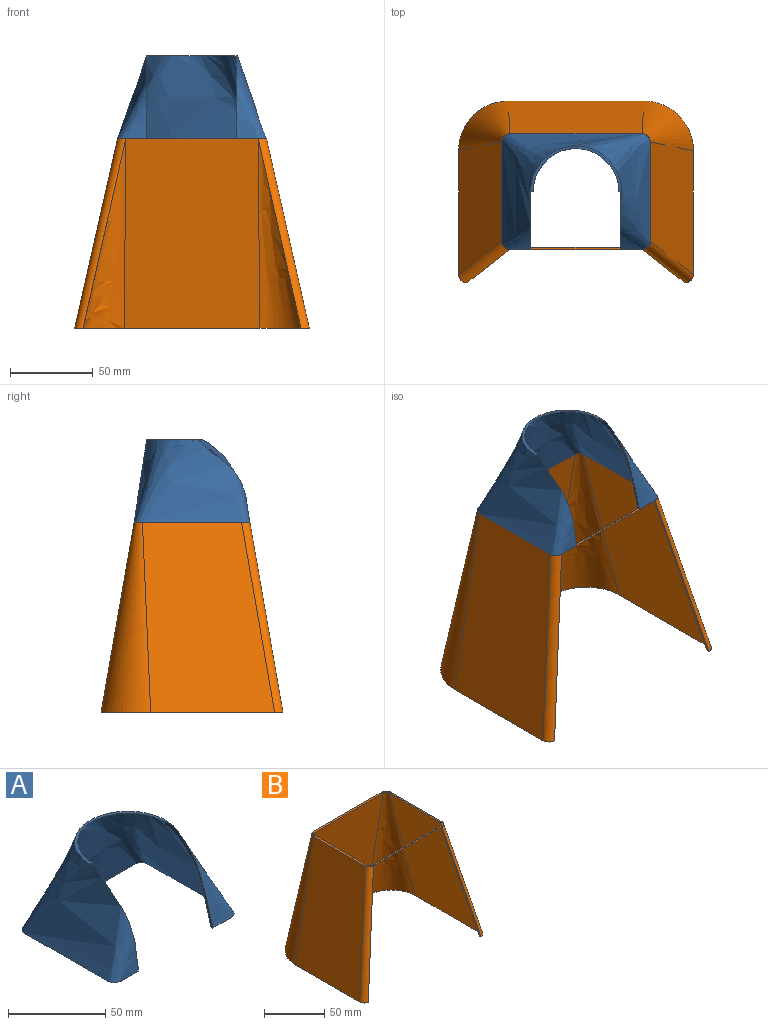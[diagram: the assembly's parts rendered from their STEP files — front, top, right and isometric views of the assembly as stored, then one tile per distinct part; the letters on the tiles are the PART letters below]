
ASSEMBLY  parts=2 mates=1
PART A: 8 faces, bbox 3360.5x2510.9x2276.9 mm
  f0: offset ~1137.38x287.71mm, area 68863mm2, adj f1,f2,f4,f5,f6,f7
  f1: plane 2316.14x2296.14mm, normal (0,0,1), area 367.9mm2, adj f0,f3,f5,f7
  f2: plane 66.45x45.38mm, normal (0,0,-1), area 137.2mm2, adj f0,f3,f4,f5,f6,f7
  f3: bspline ~90x70mm, area 9629.4mm2, adj f1,f2,f5,f7
  f4: plane 15.71x12.77mm, normal (0,1,0), area 3mm2, adj f0,f2,f5
  f5: plane 2276.15x2261.14mm, normal (-1,0,0), area 160.4mm2, adj f0,f1,f2,f3,f4
  f6: plane 2.56x0.94mm, normal (0,1,0), area 1mm2, adj f0,f2,f7
  f7: plane 50x35mm, normal (1,0,0), area 126.3mm2, adj f0,f1,f2,f3,f6
PART B: 20 faces, bbox 145x113x119.2 mm
  f0: plane 80x0.26mm, normal (0,0.99,-0.17), area 20.9mm2, adj f2,f12,f13,f17
  f1: plane 142.27x110.27mm, normal (0,0,-1), area 516.3mm2, adj f3,f4,f5,f6,f7,f8,f9,f10
  f2: plane 90.61x70.61mm, normal (0,0,1), area 469mm2, adj f0,f3,f4,f5,f6,f7,f8,f9
  f3: bspline ~116.15x66.9mm, area 3220.6mm2, adj f1,f2,f4,f9
  f4: plane 115x80mm, normal (-0.98,0,0.22), area 7958.4mm2, adj f1,f2,f3,f5
  f5: bspline ~137.75x116.15mm, area 932.3mm2, adj f1,f2,f4,f18
  f6: bspline ~137.75x116.15mm, area 932.3mm2, adj f1,f2,f7,f19
  f7: plane 115x80mm, normal (0.98,0,0.22), area 7958.4mm2, adj f1,f2,f6,f8
  f8: bspline ~116.15x113.34mm, area 3220.6mm2, adj f1,f2,f7,f9
  f9: plane 115x82mm, normal (0,0.99,0.17), area 9454.8mm2, adj f1,f2,f3,f8
  f10: offset ~118.07x33.94mm, area 2937.7mm2, adj f1,f2,f11,f16
  f11: plane 115x79.96mm, normal (0.98,0,-0.22), area 7953.3mm2, adj f1,f2,f10,f12
  f12: offset ~140.75x119.15mm, area 657mm2, adj f0,f1,f2,f11,f18
  f13: offset ~140.75x119.15mm, area 657mm2, adj f0,f1,f2,f14,f19
  f14: plane 115x79.96mm, normal (-0.98,0,-0.22), area 7953.3mm2, adj f1,f2,f13,f15
  f15: offset ~119.15x116.34mm, area 2937.8mm2, adj f1,f2,f14,f16
  f16: plane 115x82mm, normal (0,-0.99,-0.17), area 9454.3mm2, adj f1,f2,f10,f15
  f17: plane 80x1.48mm, normal (0,-0.17,-0.99), area 120mm2, adj f0,f2,f18,f19
  f18: plane 115x26mm, normal (0.98,-0.04,-0.21), area 179.2mm2, adj f1,f5,f12,f17
  f19: plane 115x26mm, normal (-0.98,-0.04,-0.21), area 179.2mm2, adj f1,f6,f13,f17
PLACE A t=(-127.21,54.77,123.93)mm
PLACE B t=(-127.21,54.77,8.93)mm
MATE fastened B.f2 <-> A.f1  axis (0,0,1) through (-127.21,54.77,123.93)mm
